# Revit family: Shower-Shower_Trim-KOHLER-Honesty-K-TLS99764
name_source: partatom
category: Plumbing Fixtures
revit_build: Autodesk Revit 2015 (Build: 20140606_1530(x64)
units: mm (PartAtom-declared; Revit-internal decimal feet)

## types (1)
- CP-Polished Chrome
    ADA Compliant = Yes
    Assembly Code = D2010700
    CW Connection = No
    Cold Water Inlet = Cold Water Inlet
    Date Modified = 04/09/2019
    Default Elevation = 42"
    Description = Rite-Temp shower valve trim with lever handle, less showerhead
    Drain Included = No
    Finish = Kohler-Metal-CP-Polished_Chrome
    Flow Rate = 0 GPM
    HW Connection = Yes
    Handle Clearance = 3 3/16"
    Height = 6 1/2"
    Hot Water Inlet = Hot Water Inlet
    Length = 4 3/8"
    Manufacturer = KOHLER Co.
    MasterFormat 1995 = 15410
    MasterFormat 2004 = 22.41.23
    Material = Premium Metal Construction
    Model = K-TLS99764-4-CP
    Pressure = 0.00 psi
    Product Documentation Link = https://www.us.kohler.com
    Product Name = Honesty
    Product Page URL = http://www.us.kohler.com
    Tempered Water Inlet = Tempered Water Inlet
    URL = https://www.us.kohler.com
    Vent Connection = No
    Waste Connection = No
    Waste Water Outlet = Waste Water Outlet
    WaterSense Certified = No
    Width = 6 1/2"

## geometry (parser evidence)
native form markers: Sweep x9
no freeform markers — native parametric forms only
